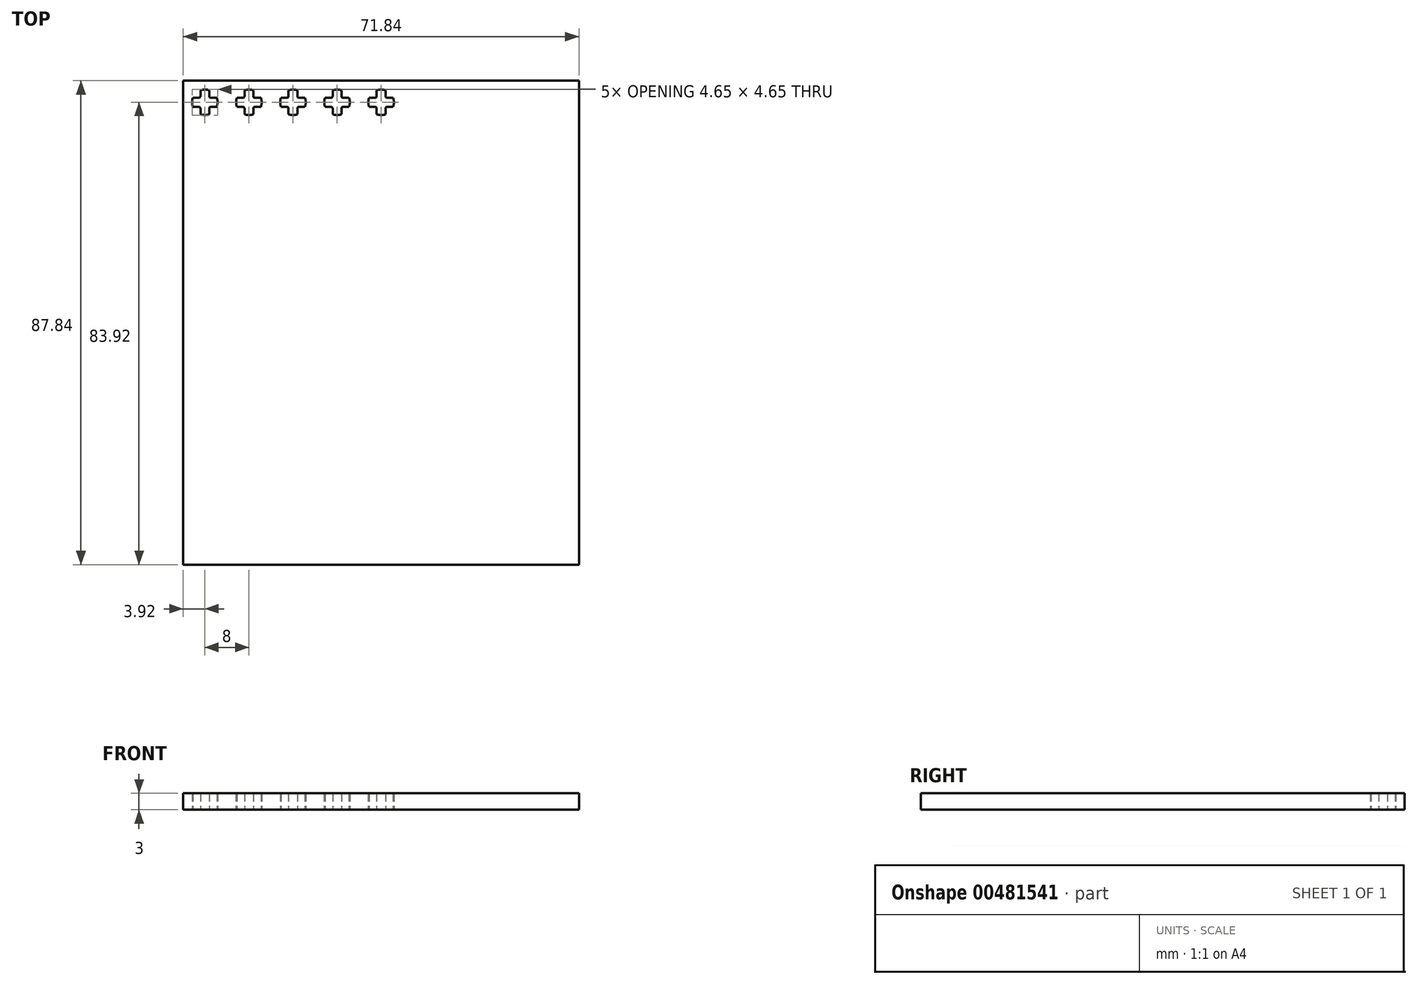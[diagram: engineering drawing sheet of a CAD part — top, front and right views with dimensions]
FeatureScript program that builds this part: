
annotation { "Feature Type Name" : "Feature", "Feature Type Description" : "" }
export const myFeature = defineFeature(function(context is Context, id is Id, definition is map)
    precondition{}
    {
        {
            var Q0;
            Q0=qCreatedBy(makeId("Top.planeOp"),FACE);
            var sketch = newSketch(context, id + "F0", { "sketchPlane" : qUnion([Q0])});
            skLineSegment(sketch, "E0.bottom", {"start": v(-36, 44) * mm, "end": v(36, 44) * mm});
            skLineSegment(sketch, "E0.top", {"start": v(-36, -44) * mm, "end": v(36, -44) * mm});
            skLineSegment(sketch, "E0.left", {"start": v(-36, 44) * mm, "end": v(-36, -44) * mm});
            skLineSegment(sketch, "E0.right", {"start": v(36, 44) * mm, "end": v(36, -44) * mm});
            skLineSegment(sketch, "E1", {"start": v(-32.8, 42.18) * mm, "end": v(-31.2, 42.18) * mm, "construction": true});
            skLineSegment(sketch, "E2", {"start": v(-31.2, 42.18) * mm, "end": v(-31.2, 41.1) * mm});
            skLineSegment(sketch, "E3", {"start": v(-30.9, 40.8) * mm, "end": v(-29.82, 40.8) * mm});
            skLineSegment(sketch, "E4", {"start": v(-29.82, 40.8) * mm, "end": v(-32, 40) * mm, "construction": true});
            skLineSegment(sketch, "E5", {"start": v(-32, 40) * mm, "end": v(-32.8, 42.18) * mm, "construction": true});
            skArc(sketch, "E6", {"start": v(-31.2, 42.18) * mm, "mid": v(-32, 42.33) * mm, "end": v(-32.8, 42.18) * mm});
            skArc(sketch, "E7", {"start": v(-31.2, 41.1) * mm, "mid": v(-31.11, 40.89) * mm, "end": v(-30.9, 40.8) * mm});
            skLineSegment(sketch, "E8", {"start": v(-31.2, 42.18) * mm, "end": v(-31.2, 40.8) * mm, "construction": true});
            skLineSegment(sketch, "E9", {"start": v(-31.2, 40.8) * mm, "end": v(-29.82, 40.8) * mm, "construction": true});
            skArc(sketch, "E10.1.0", {"start": v(-34.18, 40.8) * mm, "mid": v(-34.32, 40) * mm, "end": v(-34.18, 39.2) * mm});
            skArc(sketch, "E10.1.1", {"start": v(-33.1, 40.8) * mm, "mid": v(-32.89, 40.89) * mm, "end": v(-32.8, 41.1) * mm});
            skLineSegment(sketch, "E10.1.2", {"start": v(-34.18, 40.8) * mm, "end": v(-33.1, 40.8) * mm});
            skLineSegment(sketch, "E10.1.3", {"start": v(-32.8, 41.1) * mm, "end": v(-32.8, 42.18) * mm});
            skArc(sketch, "E10.2.0", {"start": v(-32.8, 37.82) * mm, "mid": v(-32, 37.68) * mm, "end": v(-31.2, 37.82) * mm});
            skArc(sketch, "E10.2.1", {"start": v(-32.8, 38.9) * mm, "mid": v(-32.89, 39.11) * mm, "end": v(-33.1, 39.2) * mm});
            skLineSegment(sketch, "E10.2.2", {"start": v(-32.8, 37.82) * mm, "end": v(-32.8, 38.9) * mm});
            skLineSegment(sketch, "E10.2.3", {"start": v(-33.1, 39.2) * mm, "end": v(-34.18, 39.2) * mm});
            skArc(sketch, "E10.3.0", {"start": v(-29.82, 39.2) * mm, "mid": v(-29.67, 40) * mm, "end": v(-29.82, 40.8) * mm});
            skArc(sketch, "E10.3.1", {"start": v(-30.9, 39.2) * mm, "mid": v(-31.11, 39.11) * mm, "end": v(-31.2, 38.9) * mm});
            skLineSegment(sketch, "E10.3.2", {"start": v(-29.82, 39.2) * mm, "end": v(-30.9, 39.2) * mm});
            skLineSegment(sketch, "E10.3.3", {"start": v(-31.2, 38.9) * mm, "end": v(-31.2, 37.82) * mm});
            skArc(sketch, "E11.1.0.0", {"start": v(-23.2, 42.18) * mm, "mid": v(-24, 42.33) * mm, "end": v(-24.8, 42.18) * mm});
            skArc(sketch, "E11.1.0.1", {"start": v(-22.9, 39.2) * mm, "mid": v(-23.11, 39.11) * mm, "end": v(-23.2, 38.9) * mm});
            skLineSegment(sketch, "E11.1.0.2", {"start": v(-21.82, 39.2) * mm, "end": v(-22.9, 39.2) * mm});
            skLineSegment(sketch, "E11.1.0.3", {"start": v(-25.1, 39.2) * mm, "end": v(-26.18, 39.2) * mm});
            skArc(sketch, "E11.1.0.4", {"start": v(-24.8, 38.9) * mm, "mid": v(-24.89, 39.11) * mm, "end": v(-25.1, 39.2) * mm});
            skLineSegment(sketch, "E11.1.0.5", {"start": v(-24.8, 41.1) * mm, "end": v(-24.8, 42.18) * mm});
            skLineSegment(sketch, "E11.1.0.6", {"start": v(-26.18, 40.8) * mm, "end": v(-25.1, 40.8) * mm});
            skArc(sketch, "E11.1.0.7", {"start": v(-25.1, 40.8) * mm, "mid": v(-24.89, 40.89) * mm, "end": v(-24.8, 41.1) * mm});
            skArc(sketch, "E11.1.0.8", {"start": v(-24.8, 37.82) * mm, "mid": v(-24, 37.68) * mm, "end": v(-23.2, 37.82) * mm});
            skArc(sketch, "E11.1.0.9", {"start": v(-26.18, 40.8) * mm, "mid": v(-26.32, 40) * mm, "end": v(-26.18, 39.2) * mm});
            skPoint(sketch, "E11.1.0.10", {"position": v(-24, 40) * mm});
            skLineSegment(sketch, "E11.1.0.11", {"start": v(-24.8, 37.82) * mm, "end": v(-24.8, 38.9) * mm});
            skArc(sketch, "E11.1.0.12", {"start": v(-21.82, 39.2) * mm, "mid": v(-21.67, 40) * mm, "end": v(-21.82, 40.8) * mm});
            skLineSegment(sketch, "E11.1.0.13", {"start": v(-23.2, 38.9) * mm, "end": v(-23.2, 37.82) * mm});
            skLineSegment(sketch, "E11.1.0.14", {"start": v(-23.2, 42.18) * mm, "end": v(-23.2, 41.1) * mm});
            skLineSegment(sketch, "E11.1.0.15", {"start": v(-22.9, 40.8) * mm, "end": v(-21.82, 40.8) * mm});
            skArc(sketch, "E11.1.0.16", {"start": v(-23.2, 41.1) * mm, "mid": v(-23.11, 40.89) * mm, "end": v(-22.9, 40.8) * mm});
            skArc(sketch, "E11.2.0.0", {"start": v(-15.2, 42.18) * mm, "mid": v(-16, 42.33) * mm, "end": v(-16.8, 42.18) * mm});
            skArc(sketch, "E11.2.0.1", {"start": v(-14.9, 39.2) * mm, "mid": v(-15.11, 39.11) * mm, "end": v(-15.2, 38.9) * mm});
            skLineSegment(sketch, "E11.2.0.2", {"start": v(-13.82, 39.2) * mm, "end": v(-14.9, 39.2) * mm});
            skLineSegment(sketch, "E11.2.0.3", {"start": v(-17.1, 39.2) * mm, "end": v(-18.18, 39.2) * mm});
            skArc(sketch, "E11.2.0.4", {"start": v(-16.8, 38.9) * mm, "mid": v(-16.89, 39.11) * mm, "end": v(-17.1, 39.2) * mm});
            skLineSegment(sketch, "E11.2.0.5", {"start": v(-16.8, 41.1) * mm, "end": v(-16.8, 42.18) * mm});
            skLineSegment(sketch, "E11.2.0.6", {"start": v(-18.18, 40.8) * mm, "end": v(-17.1, 40.8) * mm});
            skArc(sketch, "E11.2.0.7", {"start": v(-17.1, 40.8) * mm, "mid": v(-16.89, 40.89) * mm, "end": v(-16.8, 41.1) * mm});
            skArc(sketch, "E11.2.0.8", {"start": v(-16.8, 37.82) * mm, "mid": v(-16, 37.67) * mm, "end": v(-15.2, 37.82) * mm});
            skArc(sketch, "E11.2.0.9", {"start": v(-18.18, 40.8) * mm, "mid": v(-18.33, 40) * mm, "end": v(-18.18, 39.2) * mm});
            skPoint(sketch, "E11.2.0.10", {"position": v(-16, 40) * mm});
            skLineSegment(sketch, "E11.2.0.11", {"start": v(-16.8, 37.82) * mm, "end": v(-16.8, 38.9) * mm});
            skArc(sketch, "E11.2.0.12", {"start": v(-13.82, 39.2) * mm, "mid": v(-13.68, 40) * mm, "end": v(-13.82, 40.8) * mm});
            skLineSegment(sketch, "E11.2.0.13", {"start": v(-15.2, 38.9) * mm, "end": v(-15.2, 37.82) * mm});
            skLineSegment(sketch, "E11.2.0.14", {"start": v(-15.2, 42.18) * mm, "end": v(-15.2, 41.1) * mm});
            skLineSegment(sketch, "E11.2.0.15", {"start": v(-14.9, 40.8) * mm, "end": v(-13.82, 40.8) * mm});
            skArc(sketch, "E11.2.0.16", {"start": v(-15.2, 41.1) * mm, "mid": v(-15.11, 40.89) * mm, "end": v(-14.9, 40.8) * mm});
            skLineSegment(sketch, "E11.direction1", {"start": v(-32.8, 37.82) * mm, "end": v(-24.8, 37.82) * mm, "construction": true});
            skLineSegment(sketch, "E11.direction2", {"start": v(-32.8, 37.82) * mm, "end": v(-32.8, 29.82) * mm, "construction": true});
            skLineSegment(sketch, "E12.bottom", {"start": v(-35.92, 43.93) * mm, "end": v(35.93, 43.92) * mm});
            skLineSegment(sketch, "E12.top", {"start": v(-35.93, -43.92) * mm, "end": v(35.92, -43.93) * mm});
            skLineSegment(sketch, "E12.left", {"start": v(-35.92, 43.93) * mm, "end": v(-35.93, -43.92) * mm});
            skLineSegment(sketch, "E12.right", {"start": v(35.93, 43.92) * mm, "end": v(35.92, -43.93) * mm});
            skArc(sketch, "E13.0.3.0", {"start": v(-7.2, 42.18) * mm, "mid": v(-8, 42.33) * mm, "end": v(-8.8, 42.18) * mm});
            skArc(sketch, "E13.4.3.0", {"start": v(-6.9, 39.2) * mm, "mid": v(-7.11, 39.11) * mm, "end": v(-7.2, 38.9) * mm});
            skLineSegment(sketch, "E13.8.3.0", {"start": v(-5.82, 39.2) * mm, "end": v(-6.9, 39.2) * mm});
            skLineSegment(sketch, "E13.11.3.0", {"start": v(-9.1, 39.2) * mm, "end": v(-10.18, 39.2) * mm});
            skArc(sketch, "E13.14.3.0", {"start": v(-8.8, 38.9) * mm, "mid": v(-8.89, 39.11) * mm, "end": v(-9.1, 39.2) * mm});
            skLineSegment(sketch, "E13.18.3.0", {"start": v(-8.8, 41.1) * mm, "end": v(-8.8, 42.18) * mm});
            skLineSegment(sketch, "E13.21.3.0", {"start": v(-10.18, 40.8) * mm, "end": v(-9.1, 40.8) * mm});
            skArc(sketch, "E13.24.3.0", {"start": v(-9.1, 40.8) * mm, "mid": v(-8.89, 40.89) * mm, "end": v(-8.8, 41.1) * mm});
            skArc(sketch, "E13.28.3.0", {"start": v(-8.8, 37.82) * mm, "mid": v(-8, 37.67) * mm, "end": v(-7.2, 37.82) * mm});
            skArc(sketch, "E13.32.3.0", {"start": v(-10.18, 40.8) * mm, "mid": v(-10.33, 40) * mm, "end": v(-10.18, 39.2) * mm});
            skPoint(sketch, "E13.36.3.0", {"position": v(-8, 40) * mm});
            skLineSegment(sketch, "E13.37.3.0", {"start": v(-8.8, 37.82) * mm, "end": v(-8.8, 38.9) * mm});
            skArc(sketch, "E13.40.3.0", {"start": v(-5.82, 39.2) * mm, "mid": v(-5.68, 40) * mm, "end": v(-5.82, 40.8) * mm});
            skLineSegment(sketch, "E13.44.3.0", {"start": v(-7.2, 38.9) * mm, "end": v(-7.2, 37.82) * mm});
            skLineSegment(sketch, "E13.47.3.0", {"start": v(-7.2, 42.18) * mm, "end": v(-7.2, 41.1) * mm});
            skLineSegment(sketch, "E13.50.3.0", {"start": v(-6.9, 40.8) * mm, "end": v(-5.82, 40.8) * mm});
            skArc(sketch, "E13.53.3.0", {"start": v(-7.2, 41.1) * mm, "mid": v(-7.11, 40.89) * mm, "end": v(-6.9, 40.8) * mm});
            skArc(sketch, "E14.0.4.0", {"start": v(0.8, 42.18) * mm, "mid": v(0, 42.33) * mm, "end": v(-0.8, 42.18) * mm});
            skArc(sketch, "E14.4.4.0", {"start": v(1.1, 39.2) * mm, "mid": v(0.89, 39.11) * mm, "end": v(0.8, 38.9) * mm});
            skLineSegment(sketch, "E14.8.4.0", {"start": v(2.18, 39.2) * mm, "end": v(1.1, 39.2) * mm});
            skLineSegment(sketch, "E14.11.4.0", {"start": v(-1.1, 39.2) * mm, "end": v(-2.18, 39.2) * mm});
            skArc(sketch, "E14.14.4.0", {"start": v(-0.8, 38.9) * mm, "mid": v(-0.89, 39.11) * mm, "end": v(-1.1, 39.2) * mm});
            skLineSegment(sketch, "E14.18.4.0", {"start": v(-0.8, 41.1) * mm, "end": v(-0.8, 42.18) * mm});
            skLineSegment(sketch, "E14.21.4.0", {"start": v(-2.18, 40.8) * mm, "end": v(-1.1, 40.8) * mm});
            skArc(sketch, "E14.24.4.0", {"start": v(-1.1, 40.8) * mm, "mid": v(-0.89, 40.89) * mm, "end": v(-0.8, 41.1) * mm});
            skArc(sketch, "E14.28.4.0", {"start": v(-0.8, 37.82) * mm, "mid": v(0, 37.67) * mm, "end": v(0.8, 37.82) * mm});
            skArc(sketch, "E14.32.4.0", {"start": v(-2.18, 40.8) * mm, "mid": v(-2.33, 40) * mm, "end": v(-2.18, 39.2) * mm});
            skPoint(sketch, "E14.36.4.0", {"position": v(0, 40) * mm});
            skLineSegment(sketch, "E14.37.4.0", {"start": v(-0.8, 37.82) * mm, "end": v(-0.8, 38.9) * mm});
            skArc(sketch, "E14.40.4.0", {"start": v(2.18, 39.2) * mm, "mid": v(2.32, 40) * mm, "end": v(2.18, 40.8) * mm});
            skLineSegment(sketch, "E14.44.4.0", {"start": v(0.8, 38.9) * mm, "end": v(0.8, 37.82) * mm});
            skLineSegment(sketch, "E14.47.4.0", {"start": v(0.8, 42.18) * mm, "end": v(0.8, 41.1) * mm});
            skLineSegment(sketch, "E14.50.4.0", {"start": v(1.1, 40.8) * mm, "end": v(2.18, 40.8) * mm});
            skArc(sketch, "E14.53.4.0", {"start": v(0.8, 41.1) * mm, "mid": v(0.89, 40.89) * mm, "end": v(1.1, 40.8) * mm});
            skSolve(sketch);
        }
        {
            var Q0;
            Q0=makeQuery(id+"F0.imprint","IMPRINT",FACE,{"disambiguationData":[TD([[makeQuery(id+"F0.imprint","IMPRINT",EDGE,{"derivedFrom":sQuery(id+"F0.wireOp",EDGE,"E2")}),1.0]])]});
            extrude(context, id + "F1", {"entities" : qUnion([Q0]), "depth" : 3 * mm, "offsetDistance" : 25 * mm});
        }
    });
